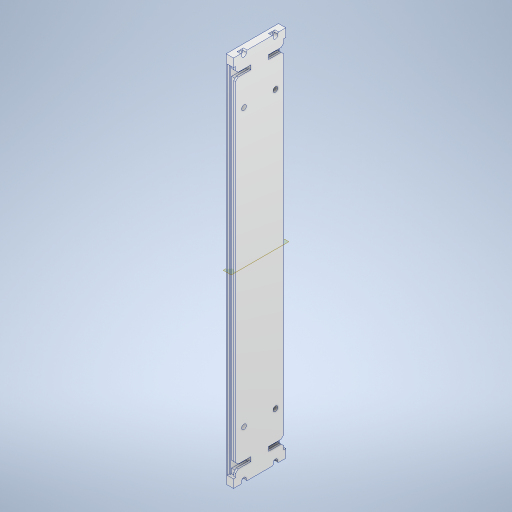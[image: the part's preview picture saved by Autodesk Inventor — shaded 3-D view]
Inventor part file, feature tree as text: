
AUTODESK INVENTOR PART (.ipt)
format: ipt  version: 2024 (Build 280153000, 153)  size: 424,960 bytes
history: native  units: mm
features: sketch x5, extrude x4, other x2, chamfer x1, hole x1, mirror x1, fillet x1
ambient origin geometry x8: Origin, YZ Plane, XZ Plane, XY Plane, X Axis, Y Axis, Z Axis, Center Point
bodies: Body1 (feature_tree)
feature tree (15):
  other  "Твердое тело1"
  extrude  "Выдавливание1"  Depth=6.5mm
  extrude  "Выдавливание3"  Depth=6.5mm
  extrude  "Выдавливание4"  Depth=2.5mm
  chamfer  "Фаска2"  Distance=4.0mm
  sketch  "Эскиз7"
  other  "РабПлоскость1"
  hole  "Отверстие1"  [1 undecoded]
  mirror  "Зеркальное отражение1"
  fillet  "Сопряжение2"  Radius=100.0mm
  extrude  "Extrusion5"  Depth=10.0mm
  sketch  "Эскиз1"
  sketch  "Эскиз5"
  sketch  "Эскиз6"
  sketch  "Sketch8"  dims[d0=14.0mm d1=6.5mm d2=6.5mm d3=2.5mm d4=4.0mm d5=2.0mm d6=100.0mm d7=50.0mm d8=712.0mm d9=0.0mm d18=16.0mm d19=0.0mm d20=16.0mm d21=100.0mm d22=0.0mm d26=356.0mm d27=100.0mm d28=0.0mm d29=4.99mm d30=2.0mm d31=45.0deg d32=5.0mm d33=20.0mm d34=20.0mm d35=5.0mm d36=92.0mm d37=92.0mm d38=5.0mm d39=5.0mm d40=4.0mm d41=4.0mm d42=5.0mm d43=6.0mm d44=9.0mm d45=7.0mm d46=90.0deg d47=8.0mm d48=20.594885mm d50=2.0mm d51=34.0mm d52=10.0mm d53=0.0mm]
note: 1 required parameter value undecoded (feature->parameter linkage not recoverable at this tier; creation-order binding heuristic only, values carry confidence <= 0.55)
